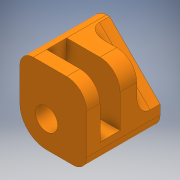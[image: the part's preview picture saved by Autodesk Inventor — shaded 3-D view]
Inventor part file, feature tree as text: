
AUTODESK INVENTOR PART (.ipt)
format: ipt  version: 2017 (Build 210142000, 142)  size: 246,784 bytes
history: native  units: mm
features: extrude x10, sketch x10, fillet x3
ambient origin geometry x8: Origin, YZ Plane, XZ Plane, XY Plane, X Axis, Y Axis, Z Axis, Center Point
bodies: Solid1 (feature_tree)
feature tree (23):
  extrude  "Extrusion1"  Depth=3.0mm
  extrude  "Extrusion2"  Depth=3.0mm
  extrude  "Extrusion3"  Depth=0.5mm TaperAngle=0.0deg
  fillet  "Fillet1"  Radius=2.0mm
  sketch  "Sketch5"  dims[d10=2.0mm d11=2.0mm]
  sketch  "Sketch7"  dims[d12=3.3333mm d15=5.8mm]
  extrude  "Extrusion8"  Depth=2.0mm
  extrude  "Extrusion10"  Depth=5.8mm
  extrude  "Extrusion11"  Depth=5.5mm TaperAngle=0.0deg
  extrude  "Extrusion12"  Depth=0.25mm TaperAngle=0.0deg
  fillet  "Fillet3"  Radius=0.25mm
  extrude  "Extrusion14"  Depth=0.2mm TaperAngle=0.0deg
  extrude  "Extrusion15"  Depth=2.0mm
  extrude  "Extrusion16"  [1 undecoded]
  fillet  "Fillet5"  [1 undecoded]
  sketch  "Sketch1"  dims[d0=5.0mm d1=3.0mm]
  sketch  "Sketch2"  dims[d2=4.0mm d3=3.0mm]
  sketch  "Sketch3"  dims[d4=5.5mm d5=0.0mm d6=0.5mm d7=0.0mm d8=2.0mm d9=0.0mm]
  sketch  "Sketch11"  dims[d25=5.5mm d26=0.0mm d30=1.3mm d31=0.0mm]
  sketch  "Sketch12"  dims[d32=6.0mm d33=0.0mm d34=1.0mm d35=0.0mm d36=0.25mm]
  sketch  "Sketch14"  dims[d41=0.3mm d42=0.0mm d43=0.2mm d44=0.0mm]
  sketch  "Sketch15"  dims[d45=0.2mm d46=0.0mm d47=2.0mm]
  sketch  "Sketch16"  dims[d48=2.0mm d49=0.0mm]
note: 2 required parameter values undecoded (feature->parameter linkage not recoverable at this tier; creation-order binding heuristic only, values carry confidence <= 0.55)
